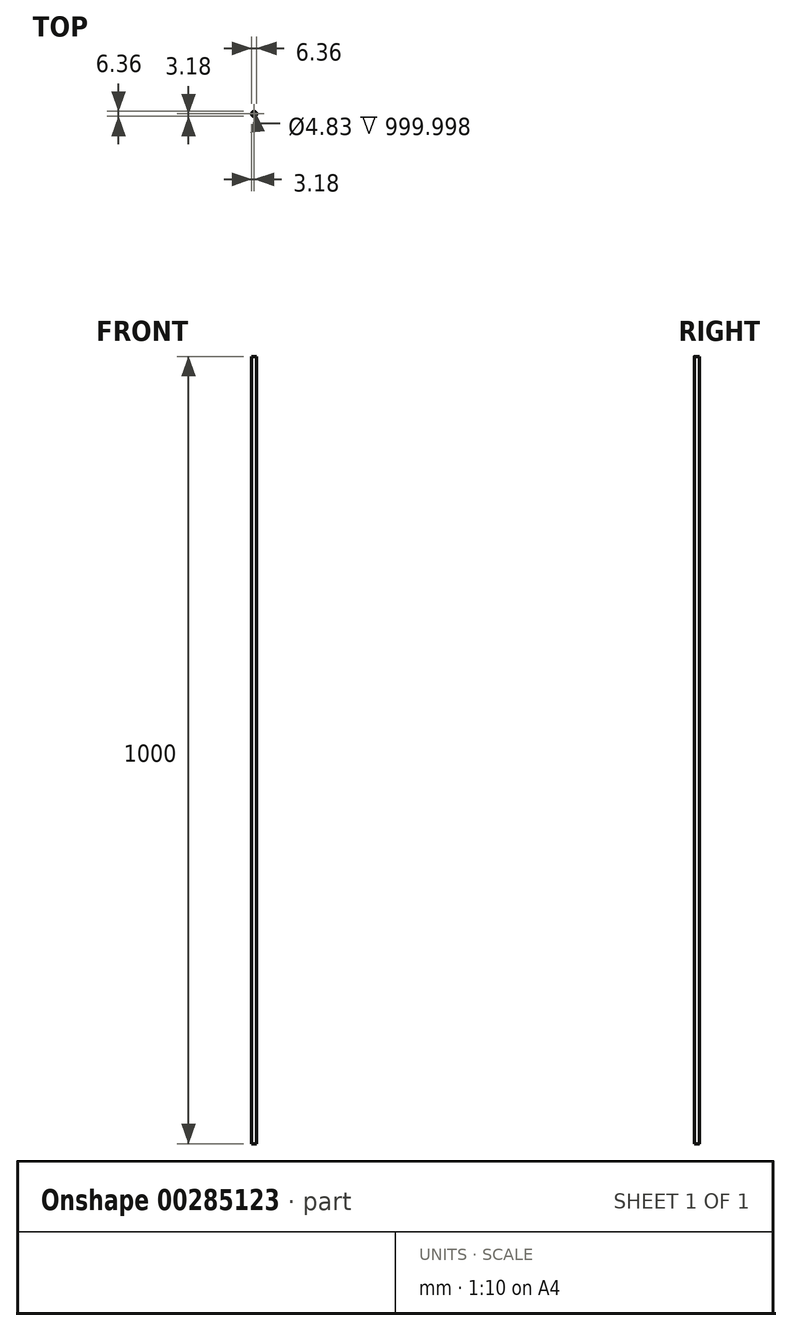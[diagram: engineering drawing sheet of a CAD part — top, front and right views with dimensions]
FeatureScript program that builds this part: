
annotation { "Feature Type Name" : "Feature", "Feature Type Description" : "" }
export const myFeature = defineFeature(function(context is Context, id is Id, definition is map)
    precondition{}
    {
        {
            var Q0;
            Q0=qCreatedBy(makeId("Top.planeOp"),FACE);
            var sketch = newSketch(context, id + "F0", { "sketchPlane" : qUnion([Q0])});
            skCircle(sketch, "E0", {"center": v(0, 0) * mm, "radius": 3.18 * mm});
            skCircle(sketch, "E1", {"center": v(0, 0) * mm, "radius": 2.41 * mm});
            skSolve(sketch);
        }
        {
            var Q0;
            Q0=makeQuery(id+"F0.imprint","IMPRINT",FACE,{"disambiguationData":[TD([[makeQuery(id+"F0.imprint","IMPRINT",EDGE,{"derivedFrom":sQuery(id+"F0.wireOp",EDGE,"E0")}),1.0]])]});
            extrude(context, id + "F1", {"entities" : qUnion([Q0]), "depth" : 1000 * mm});
        }
    });
